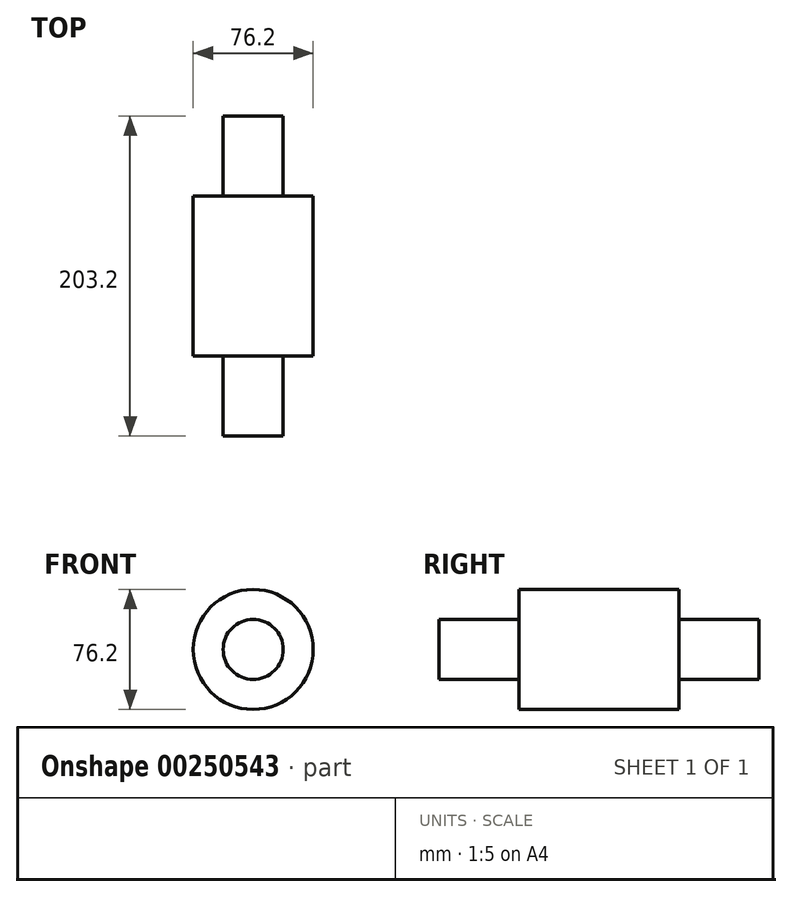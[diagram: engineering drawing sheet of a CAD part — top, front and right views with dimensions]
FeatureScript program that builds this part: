
annotation { "Feature Type Name" : "Feature", "Feature Type Description" : "" }
export const myFeature = defineFeature(function(context is Context, id is Id, definition is map)
    precondition{}
    {
        {
            var Q0;
            Q0=qCreatedBy(makeId("Front.planeOp"),FACE);
            var sketch = newSketch(context, id + "F0", { "sketchPlane" : qUnion([Q0])});
            skCircle(sketch, "E0", {"center": v(0, 0) * mm, "radius": 38.1 * mm});
            skSolve(sketch);
        }
        {
            var Q0;
            Q0=makeQuery(id+"F0.imprint","IMPRINT",FACE,{"disambiguationData":[TD([[makeQuery(id+"F0.imprint","IMPRINT",EDGE,{"derivedFrom":sQuery(id+"F0.wireOp",EDGE,"E0")}),1.0]])]});
            extrude(context, id + "F1", {"entities" : qUnion([Q0]), "endBound" : BoundingType.SYMMETRIC, "depth" : 101.6 * mm});
        }
        {
            var Q0;
            Q0=qCreatedBy(makeId("Front.planeOp"),FACE);
            var sketch = newSketch(context, id + "F2", { "sketchPlane" : qUnion([Q0])});
            skCircle(sketch, "E1", {"center": v(0, 0) * mm, "radius": 19.05 * mm});
            skSolve(sketch);
        }
        {
            var Q0;
            Q0 = qSketchRegion(id + "F2", true);
            extrude(context, id + "F3", {"entities" : qUnion([Q0]), "operationType" : NewBodyOperationType.ADD, "endBound" : BoundingType.SYMMETRIC, "depth" : 203.2 * mm});
        }
    });
